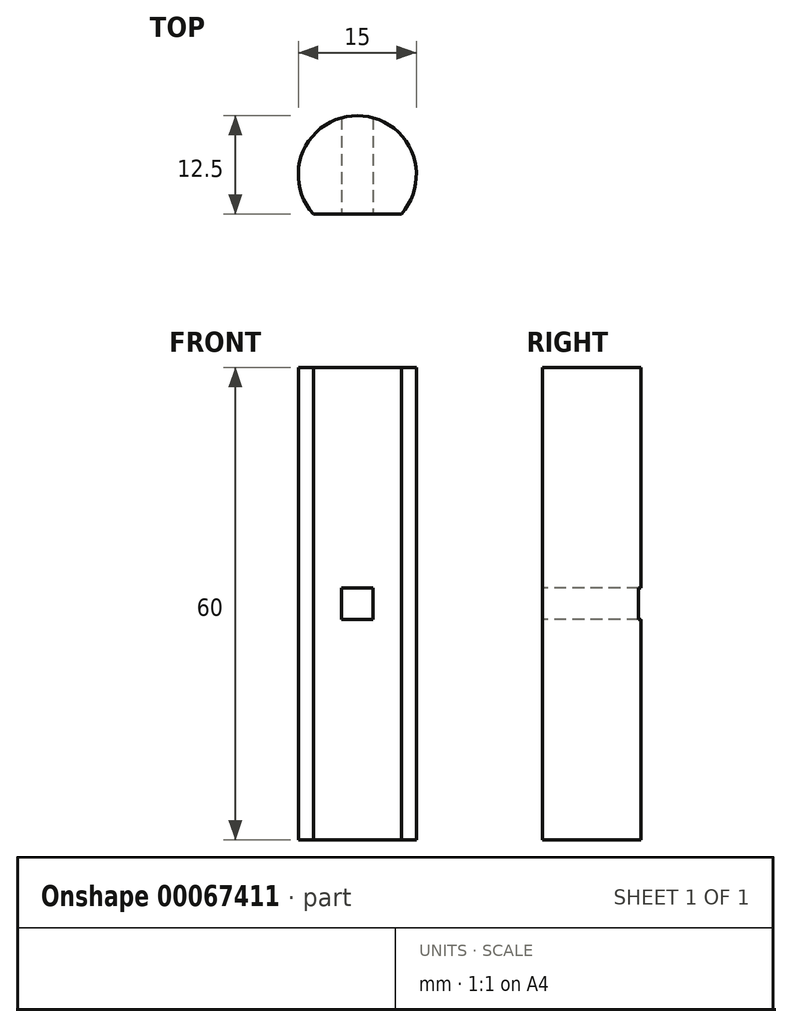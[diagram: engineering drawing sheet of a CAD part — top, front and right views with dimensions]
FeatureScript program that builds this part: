
annotation { "Feature Type Name" : "Feature", "Feature Type Description" : "" }
export const myFeature = defineFeature(function(context is Context, id is Id, definition is map)
    precondition{}
    {
        {
            var Q0;
            Q0=qCreatedBy(makeId("Top.planeOp"),FACE);
            var sketch = newSketch(context, id + "F0", { "sketchPlane" : qUnion([Q0])});
            skArc(sketch, "E0", {"start": v(5.6, -5) * mm, "mid": v(0, 7.5) * mm, "end": v(-5.6, -5) * mm});
            skLineSegment(sketch, "E1", {"start": v(-5.6, -5) * mm, "end": v(5.6, -5) * mm});
            skSolve(sketch);
        }
        {
            var Q0;
            Q0=makeQuery(id+"F0.imprint","IMPRINT",FACE,{"disambiguationData":[TD([[makeQuery(id+"F0.imprint","IMPRINT",EDGE,{"derivedFrom":sQuery(id+"F0.wireOp",EDGE,"E0")}),1.0]])]});
            extrude(context, id + "F1", {"entities" : qUnion([Q0]), "depth" : 60 * mm});
        }
        {
            var Q0;
            Q0=qCreatedBy(makeId("Front.planeOp"),FACE);
            var sketch = newSketch(context, id + "F2", { "sketchPlane" : qUnion([Q0])});
            skLineSegment(sketch, "E2.bottom", {"start": v(-2, 32) * mm, "end": v(2, 32) * mm});
            skLineSegment(sketch, "E2.top", {"start": v(-2, 28) * mm, "end": v(2, 28) * mm});
            skLineSegment(sketch, "E2.left", {"start": v(-2, 32) * mm, "end": v(-2, 28) * mm});
            skLineSegment(sketch, "E2.right", {"start": v(2, 32) * mm, "end": v(2, 28) * mm});
            skPoint(sketch, "E2.middle", {"position": v(0, 30) * mm});
            skSolve(sketch);
        }
        {
            var Q0;
            Q0=qSketchRegion(id+"F2",true);
            extrude(context, id + "F3", {"entities" : qUnion([Q0]), "operationType" : NewBodyOperationType.REMOVE, "endBound" : BoundingType.SYMMETRIC, "oppositeDirection" : true, "depth" : 20 * mm});
        }
    });
